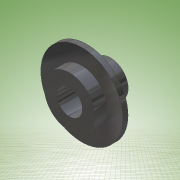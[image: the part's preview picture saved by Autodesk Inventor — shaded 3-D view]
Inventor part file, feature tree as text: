
AUTODESK INVENTOR PART (.ipt)
format: ipt  version: 2011 (Build 150239000, 239)  size: 126,464 bytes
history: native  units: in
note: dims shown in document units (in); Inventor stores cm internally (conversion verified against a paired STEP export)
features: extrude x5, sketch x5
ambient origin geometry x8: Origin, YZ Plane, XZ Plane, XY Plane, X Axis, Y Axis, Z Axis, Center Point
bodies: Solid1 (feature_tree)
feature tree (10):
  extrude  "Extrusion1"  Depth=0.25in TaperAngle=0.0deg
  extrude  "Extrusion2"  Depth=0.075in TaperAngle=0.0deg
  extrude  "Extrusion3"  Depth=0.075in TaperAngle=0.0deg
  extrude  "Extrusion4"  Depth=0.138in TaperAngle=0.0deg
  extrude  "Extrusion5"  [1 undecoded]
  sketch  "Sketch1"  dims[d0=0.5in d1=0.25in d2=0.0in]
  sketch  "Sketch2"  dims[d3=0.308in d4=0.075in d5=0.0in]
  sketch  "Sketch3"  dims[d6=0.1565in d7=0.075in d8=0.0in]
  sketch  "Sketch4"  dims[d9=0.216in d10=0.138in d11=0.0in]
  sketch  "Sketch5"  dims[d12=0.005in d13=0.0in]
note: 1 required parameter value undecoded (feature->parameter linkage not recoverable at this tier; creation-order binding heuristic only, values carry confidence <= 0.55)
